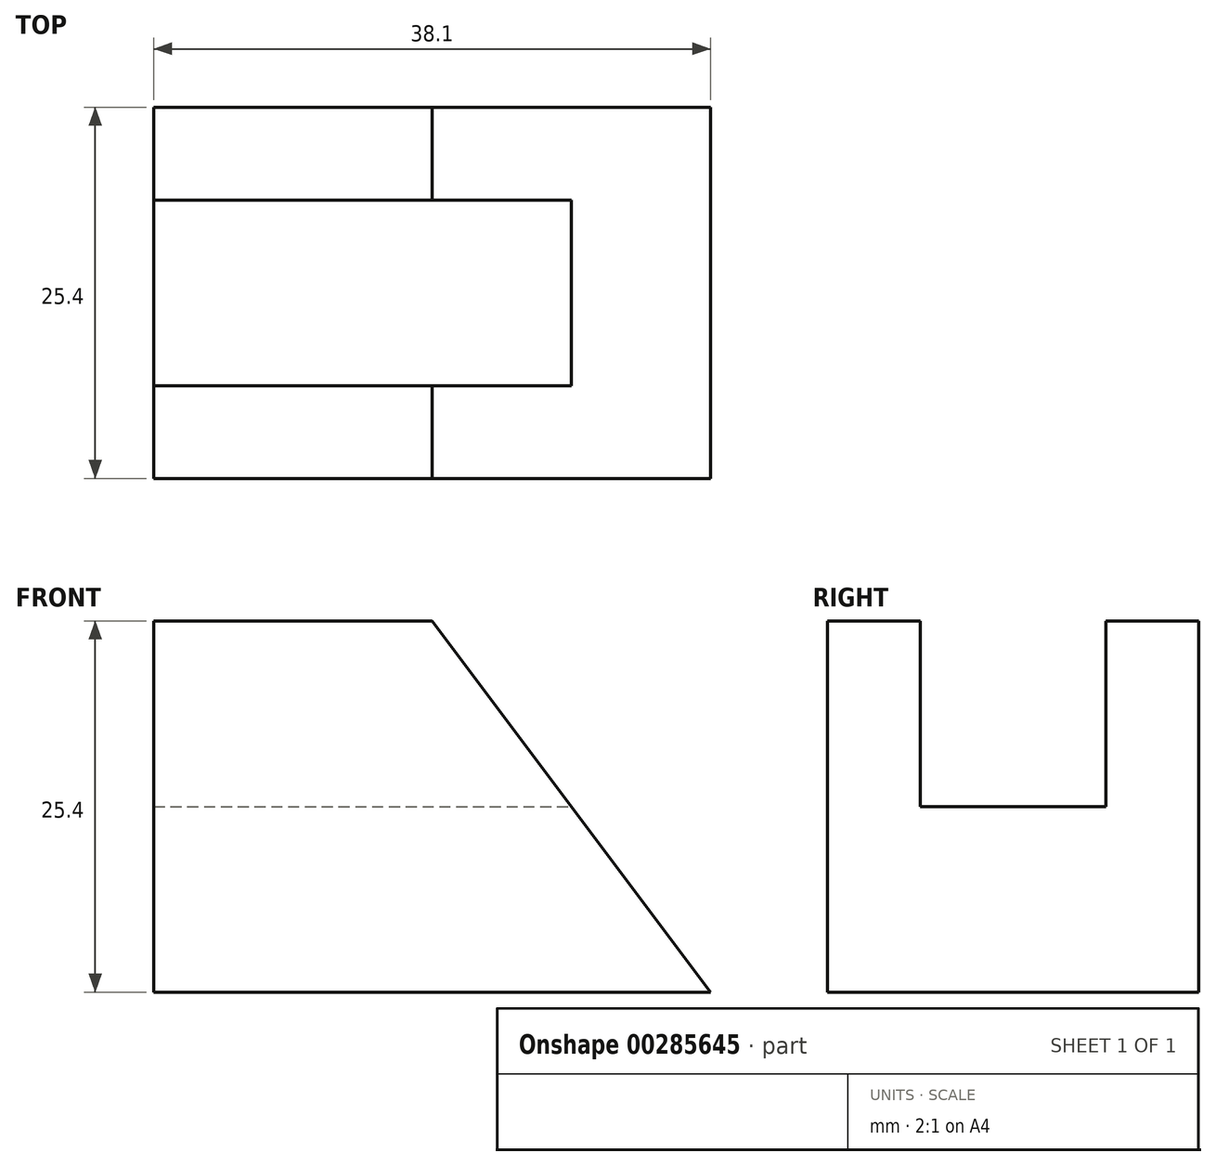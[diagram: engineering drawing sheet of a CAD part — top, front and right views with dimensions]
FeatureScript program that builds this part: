
annotation { "Feature Type Name" : "Feature", "Feature Type Description" : "" }
export const myFeature = defineFeature(function(context is Context, id is Id, definition is map)
    precondition{}
    {
        {
            var Q0;
            Q0=qCreatedBy(makeId("Front.planeOp"),FACE);
            var sketch = newSketch(context, id + "F0", { "sketchPlane" : qUnion([Q0])});
            skLineSegment(sketch, "E0", {"start": v(0, 0) * mm, "end": v(0, 25.4) * mm});
            skLineSegment(sketch, "E1", {"start": v(0, 25.4) * mm, "end": v(19.05, 25.4) * mm});
            skLineSegment(sketch, "E2", {"start": v(19.05, 25.4) * mm, "end": v(38.1, 0) * mm});
            skLineSegment(sketch, "E3", {"start": v(38.1, 0) * mm, "end": v(0, 0) * mm});
            skSolve(sketch);
        }
        {
            var Q0;
            Q0 = qSketchRegion(id + "F0", true);
            extrude(context, id + "F1", {"entities" : qUnion([Q0]), "endBound" : BoundingType.SYMMETRIC, "oppositeDirection" : true, "depth" : 25.4 * mm});
        }
        {
            var Q0;
            Q0=qCreatedBy(makeId("Front.planeOp"),FACE);
            var sketch = newSketch(context, id + "F2", { "sketchPlane" : qUnion([Q0])});
            skLineSegment(sketch, "E4", {"start": v(0, 25.4) * mm, "end": v(0, 12.7) * mm});
            skLineSegment(sketch, "E5", {"start": v(0, 12.7) * mm, "end": v(28.58, 12.7) * mm});
            skLineSegment(sketch, "E6", {"start": v(28.57, 12.7) * mm, "end": v(19.05, 25.4) * mm});
            skLineSegment(sketch, "E7", {"start": v(19.05, 25.4) * mm, "end": v(0, 25.4) * mm});
            skSolve(sketch);
        }
        {
            var Q0;
            Q0 = qSketchRegion(id + "F2", true);
            extrude(context, id + "F3", {"entities" : qUnion([Q0]), "operationType" : NewBodyOperationType.REMOVE, "endBound" : BoundingType.SYMMETRIC, "depth" : 12.7 * mm});
        }
    });
